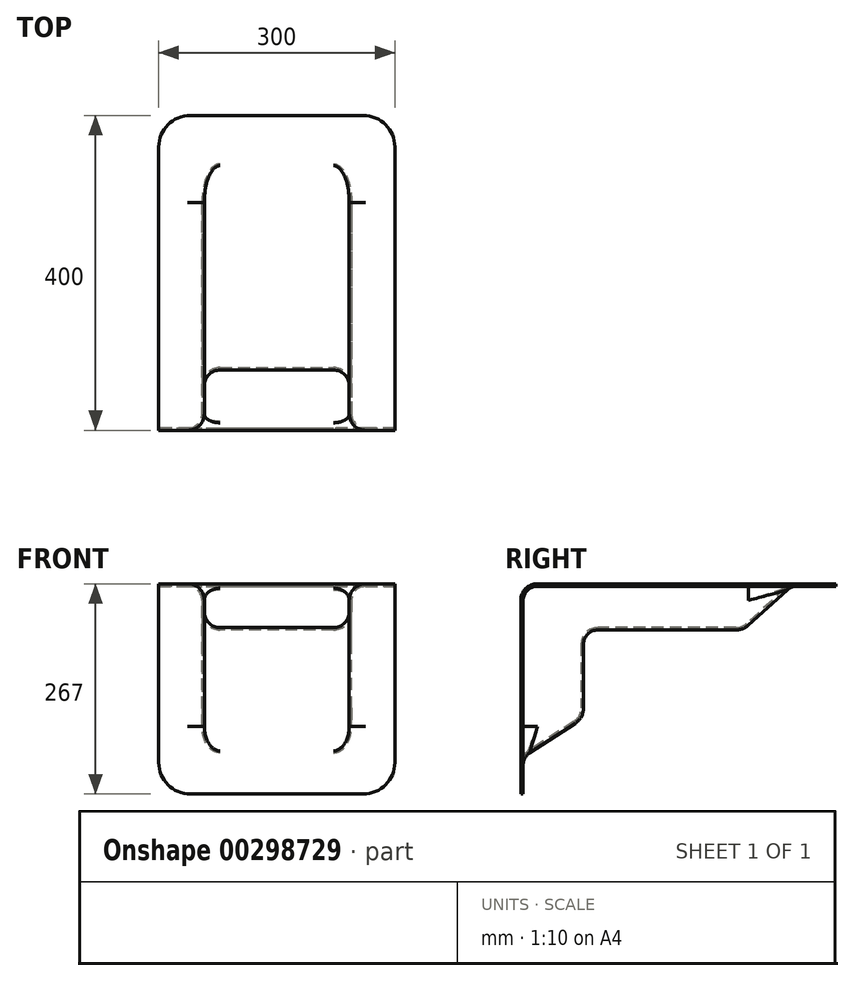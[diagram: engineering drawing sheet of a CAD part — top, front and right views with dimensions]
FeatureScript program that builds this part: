
annotation { "Feature Type Name" : "Feature", "Feature Type Description" : "" }
export const myFeature = defineFeature(function(context is Context, id is Id, definition is map)
    precondition{}
    {
        {
            var Q0;
            Q0=qCreatedBy(makeId("Top.planeOp"),FACE);
            var sketch = newSketch(context, id + "F0", { "sketchPlane" : qUnion([Q0])});
            skLineSegment(sketch, "E0.bottom", {"start": v(0, 0) * mm, "end": v(150, 0) * mm});
            skLineSegment(sketch, "E0.top", {"start": v(0, 400) * mm, "end": v(150, 400) * mm});
            skLineSegment(sketch, "E0.left", {"start": v(0, 0) * mm, "end": v(0, 400) * mm});
            skLineSegment(sketch, "E0.right", {"start": v(150, 0) * mm, "end": v(150, 400) * mm});
            skSolve(sketch);
        }
        {
            var Q0;
            Q0=makeQuery(id+"F0.imprint","IMPRINT",FACE,{"disambiguationData":[TD([[makeQuery(id+"F0.imprint","IMPRINT",EDGE,{"derivedFrom":sQuery(id+"F0.wireOp",EDGE,"E0.bottom")}),1.0]])]});
            extrude(context, id + "F1", {"entities" : qUnion([Q0]), "depth" : 267 * mm, "offsetDistance" : 25 * mm});
        }
        {
            var Q0;
            Q0=makeQuery(id+"F1.opExtrude","SWEPT_FACE",FACE,{"disambiguationData":[OSD([sQuery(id+"F0.wireOp",EDGE,"E0.left")])]});
            var sketch = newSketch(context, id + "F2", { "sketchPlane" : qUnion([Q0])});
            skLineSegment(sketch, "E1", {"start": v(-342.47, 267) * mm, "end": v(-280.98, 211.4) * mm});
            skLineSegment(sketch, "E2", {"start": v(-280.98, 211.4) * mm, "end": v(-76.7, 211.4) * mm});
            skLineSegment(sketch, "E3", {"start": v(-76.7, 211.4) * mm, "end": v(-76.7, 98.29) * mm});
            skLineSegment(sketch, "E4", {"start": v(-76.7, 98.29) * mm, "end": v(0, 48.54) * mm});
            skSolve(sketch);
        }
        {
            var Q0;
            {var subQ1=sQuery(id+"F2.wireOp",EDGE,"E1");Q0=makeQuery(id+"F2.imprint","IMPRINT",FACE,{"disambiguationData":[TD([[makeQuery(id+"F2.imprint","IMPRINT",EDGE,{"derivedFrom":subQ1}),1.0]])]});}
            extrude(context, id + "F3", {"entities" : qUnion([Q0]), "operationType" : NewBodyOperationType.REMOVE, "oppositeDirection" : true, "depth" : 92 * mm, "offsetDistance" : 25 * mm});
        }
        {
            var Q0;
            Q0=makeQuery(id+"F5.opFillet","BLEND_EDGE",EDGE,{"blendedFrom":[makeQuery(id+"F3.boolean.opBoolean","COPY",EDGE,{"derivedFrom":makeQuery(id+"F3.opExtrude","CAP_EDGE",EDGE,{"disambiguationData":[OSD([sQuery(id+"F2.wireOp",EDGE,"E1")])],"isStart":false})}),makeQuery(id+"F1.opExtrude","CAP_FACE",FACE,{"disambiguationData":[OSD([sQuery(id+"F0.wireOp",EDGE,"E0.bottom"),sQuery(id+"F0.wireOp",EDGE,"E0.top"),sQuery(id+"F0.wireOp",EDGE,"E0.left"),sQuery(id+"F0.wireOp",EDGE,"E0.right")])],"isStart":false})],"blendedInto":[makeQuery(id+"F1.opExtrude","CAP_FACE",FACE,{"disambiguationData":[OSD([sQuery(id+"F0.wireOp",EDGE,"E0.bottom"),sQuery(id+"F0.wireOp",EDGE,"E0.top"),sQuery(id+"F0.wireOp",EDGE,"E0.left"),sQuery(id+"F0.wireOp",EDGE,"E0.right")])],"isStart":false})]});
            var Q1;
            Q1=makeQuery(id+"F5.opFillet","BLEND_EDGE",EDGE,{"blendedFrom":[makeQuery(id+"F3.boolean.opBoolean","COPY",EDGE,{"derivedFrom":makeQuery(id+"F3.opExtrude","CAP_EDGE",EDGE,{"disambiguationData":[OSD([sQuery(id+"F2.wireOp",EDGE,"E4")])],"isStart":false})}),makeQuery(id+"F1.opExtrude","SWEPT_FACE",FACE,{"disambiguationData":[OSD([sQuery(id+"F0.wireOp",EDGE,"E0.bottom")])]})],"blendedInto":[makeQuery(id+"F1.opExtrude","SWEPT_FACE",FACE,{"disambiguationData":[OSD([sQuery(id+"F0.wireOp",EDGE,"E0.bottom")])]})]});
            var Q2;
            Q2=makeQuery(id+"F5.opFillet","BLEND_EDGE",EDGE,{"blendedFrom":[makeQuery(id+"F3.boolean.opBoolean","COPY",EDGE,{"derivedFrom":makeQuery(id+"F3.opExtrude","CAP_EDGE",EDGE,{"disambiguationData":[OSD([sQuery(id+"F2.wireOp",EDGE,"E2")])],"isStart":false})}),makeQuery(id+"F3.boolean.opBoolean","COPY",EDGE,{"derivedFrom":makeQuery(id+"F3.opExtrude","CAP_EDGE",EDGE,{"disambiguationData":[OSD([sQuery(id+"F2.wireOp",EDGE,"E3")])],"isStart":false})})],"blendedInto":[]});
            var Q3;
            Q3=makeQuery(id+"F1.opExtrude","CAP_EDGE",EDGE,{"disambiguationData":[OSD([sQuery(id+"F0.wireOp",EDGE,"E0.bottom")])],"isStart":false});
            var Q4;
            Q4=makeQuery(id+"F3.boolean.opBoolean","COPY",EDGE,{"derivedFrom":makeQuery(id+"F3.opExtrude","SWEPT_EDGE",EDGE,{"disambiguationData":[OSD([sQuery(id+"F2.wireOp",EDGE,"E2"),sQuery(id+"F2.wireOp",EDGE,"E3")])]})});
            fillet(context, id + "F4", {"entities" : qUnion([Q0, Q1, Q2, Q3, Q4]), "radius" : 21 * mm, "tangentPropagation" : true, "allowEdgeOverflow" : false});
        }
        {
            var Q0;
            Q0=makeQuery(id+"F3.boolean.opBoolean","COPY",EDGE,{"derivedFrom":makeQuery(id+"F3.opExtrude","SWEPT_EDGE",EDGE,{"disambiguationData":[OSD([sQuery(id+"F2.wireOp",EDGE,"E1"),sQuery(id+"F2.wireOp",EDGE,"E2")])]})});
            var Q1;
            Q1=makeQuery(id+"F3.boolean.opBoolean","COPY",EDGE,{"derivedFrom":makeQuery(id+"F3.opExtrude","SWEPT_EDGE",EDGE,{"disambiguationData":[OSD([sQuery(id+"F2.wireOp",EDGE,"E3"),sQuery(id+"F2.wireOp",EDGE,"E4")])]})});
            var Q2;
            Q2=makeQuery(id+"F3.boolean.opBoolean","COPY",EDGE,{"derivedFrom":makeQuery(id+"F3.opExtrude","CAP_EDGE",EDGE,{"disambiguationData":[OSD([sQuery(id+"F2.wireOp",EDGE,"E2")])],"isStart":false})});
            var Q3;
            Q3=makeQuery(id+"F3.boolean.opBoolean","COPY",EDGE,{"derivedFrom":makeQuery(id+"F3.opExtrude","CAP_EDGE",EDGE,{"disambiguationData":[OSD([sQuery(id+"F2.wireOp",EDGE,"E1")])],"isStart":false})});
            var Q4;
            Q4=makeQuery(id+"F3.boolean.opBoolean","COPY",EDGE,{"derivedFrom":makeQuery(id+"F3.opExtrude","CAP_EDGE",EDGE,{"disambiguationData":[OSD([sQuery(id+"F2.wireOp",EDGE,"E4")])],"isStart":false})});
            fillet(context, id + "F5", {"entities" : qUnion([Q0, Q1, Q2, Q3, Q4]), "radius" : 20 * mm, "tangentPropagation" : true, "allowEdgeOverflow" : false});
        }
        {
            var Q0;
            Q0=makeQuery(id+"F5.opFillet","BLEND_EDGE",EDGE,{"blendedFrom":[makeQuery(id+"F3.boolean.opBoolean","COPY",EDGE,{"derivedFrom":makeQuery(id+"F3.opExtrude","CAP_EDGE",EDGE,{"disambiguationData":[OSD([sQuery(id+"F2.wireOp",EDGE,"E1")])],"isStart":false})}),makeQuery(id+"F1.opExtrude","CAP_FACE",FACE,{"disambiguationData":[OSD([sQuery(id+"F0.wireOp",EDGE,"E0.bottom"),sQuery(id+"F0.wireOp",EDGE,"E0.top"),sQuery(id+"F0.wireOp",EDGE,"E0.left"),sQuery(id+"F0.wireOp",EDGE,"E0.right")])],"isStart":false})],"blendedInto":[makeQuery(id+"F1.opExtrude","CAP_FACE",FACE,{"disambiguationData":[OSD([sQuery(id+"F0.wireOp",EDGE,"E0.bottom"),sQuery(id+"F0.wireOp",EDGE,"E0.top"),sQuery(id+"F0.wireOp",EDGE,"E0.left"),sQuery(id+"F0.wireOp",EDGE,"E0.right")])],"isStart":false})]});
            fillet(context, id + "F6", {"entities" : qUnion([Q0]), "radius" : 21 * mm, "tangentPropagation" : true, "allowEdgeOverflow" : false});
        }
        {
            var Q0;
            Q0=makeQuery(id+"F1.opExtrude","CAP_EDGE",EDGE,{"disambiguationData":[OSD([sQuery(id+"F0.wireOp",EDGE,"E0.right")])],"isStart":true});
            var Q1;
            Q1=makeQuery(id+"F1.opExtrude","SWEPT_EDGE",EDGE,{"disambiguationData":[OSD([sQuery(id+"F0.wireOp",EDGE,"E0.top"),sQuery(id+"F0.wireOp",EDGE,"E0.right")])]});
            fillet(context, id + "F7", {"entities" : qUnion([Q0, Q1]), "radius" : 40 * mm, "tangentPropagation" : true, "allowEdgeOverflow" : false});
        }
        {
            var Q0;
            Q0=makeQuery(id+"F1.opExtrude","SWEPT_BODY",BODY,{"disambiguationData":[OSD([sQuery(id+"F0.wireOp",EDGE,"E0.bottom"),sQuery(id+"F0.wireOp",EDGE,"E0.top"),sQuery(id+"F0.wireOp",EDGE,"E0.left"),sQuery(id+"F0.wireOp",EDGE,"E0.right")])]});
            var Q1;
            Q1=qCreatedBy(makeId("Right.planeOp"),FACE);
            mirror(context, id + "F8", {"operationType" : NewBodyOperationType.ADD, "entities" : qUnion([Q0]), "mirrorPlane" : qUnion([Q1])});
        }
        {
            var Q0;
            {var subQ0=makeQuery(id+"F1.opExtrude","SWEPT_FACE",FACE,{"disambiguationData":[OSD([sQuery(id+"F0.wireOp",EDGE,"E0.top")])]});Q0=makeQuery(id+"F8.boolean.opBoolean","MERGE",FACE,{"derivedFrom":[subQ0,makeQuery(id+"F8.opPattern","COPY",FACE,{"derivedFrom":subQ0,"instanceName":"1"})]});}
            var Q1;
            {var subQ0=makeQuery(id+"F1.opExtrude","CAP_FACE",FACE,{"disambiguationData":[OSD([sQuery(id+"F0.wireOp",EDGE,"E0.bottom"),sQuery(id+"F0.wireOp",EDGE,"E0.top"),sQuery(id+"F0.wireOp",EDGE,"E0.left"),sQuery(id+"F0.wireOp",EDGE,"E0.right")])],"isStart":true});Q1=makeQuery(id+"F8.boolean.opBoolean","MERGE",FACE,{"derivedFrom":[subQ0,makeQuery(id+"F8.opPattern","COPY",FACE,{"derivedFrom":subQ0,"instanceName":"1"})]});}
            var Q2;
            Q2=makeQuery(id+"F8.opPattern","COPY",FACE,{"derivedFrom":makeQuery(id+"F7.opFillet","BLEND_FACE",FACE,{"disambiguationData":[OSD([sQuery(id+"F0.wireOp",EDGE,"E0.right")])]}),"instanceName":"1"});
            var Q3;
            Q3=makeQuery(id+"F8.opPattern","COPY",FACE,{"derivedFrom":makeQuery(id+"F7.opFillet","BLEND_FACE",FACE,{"disambiguationData":[OSD([sQuery(id+"F0.wireOp",EDGE,"E0.top"),sQuery(id+"F0.wireOp",EDGE,"E0.right")])]}),"instanceName":"1"});
            var Q4;
            Q4=makeQuery(id+"F8.opPattern","COPY",FACE,{"derivedFrom":makeQuery(id+"F1.opExtrude","SWEPT_FACE",FACE,{"disambiguationData":[OSD([sQuery(id+"F0.wireOp",EDGE,"E0.right")])]}),"instanceName":"1"});
            var Q5;
            Q5=makeQuery(id+"F1.opExtrude","SWEPT_FACE",FACE,{"disambiguationData":[OSD([sQuery(id+"F0.wireOp",EDGE,"E0.right")])]});
            var Q6;
            Q6=makeQuery(id+"F7.opFillet","BLEND_FACE",FACE,{"disambiguationData":[OSD([sQuery(id+"F0.wireOp",EDGE,"E0.top"),sQuery(id+"F0.wireOp",EDGE,"E0.right")])]});
            var Q7;
            Q7=makeQuery(id+"F7.opFillet","BLEND_FACE",FACE,{"disambiguationData":[OSD([sQuery(id+"F0.wireOp",EDGE,"E0.right")])]});
            shell(context, id + "F9", {"entities" : qUnion([Q0, Q1, Q2, Q3, Q4, Q5, Q6, Q7]), "thickness" : 3 * mm});
        }
    });
